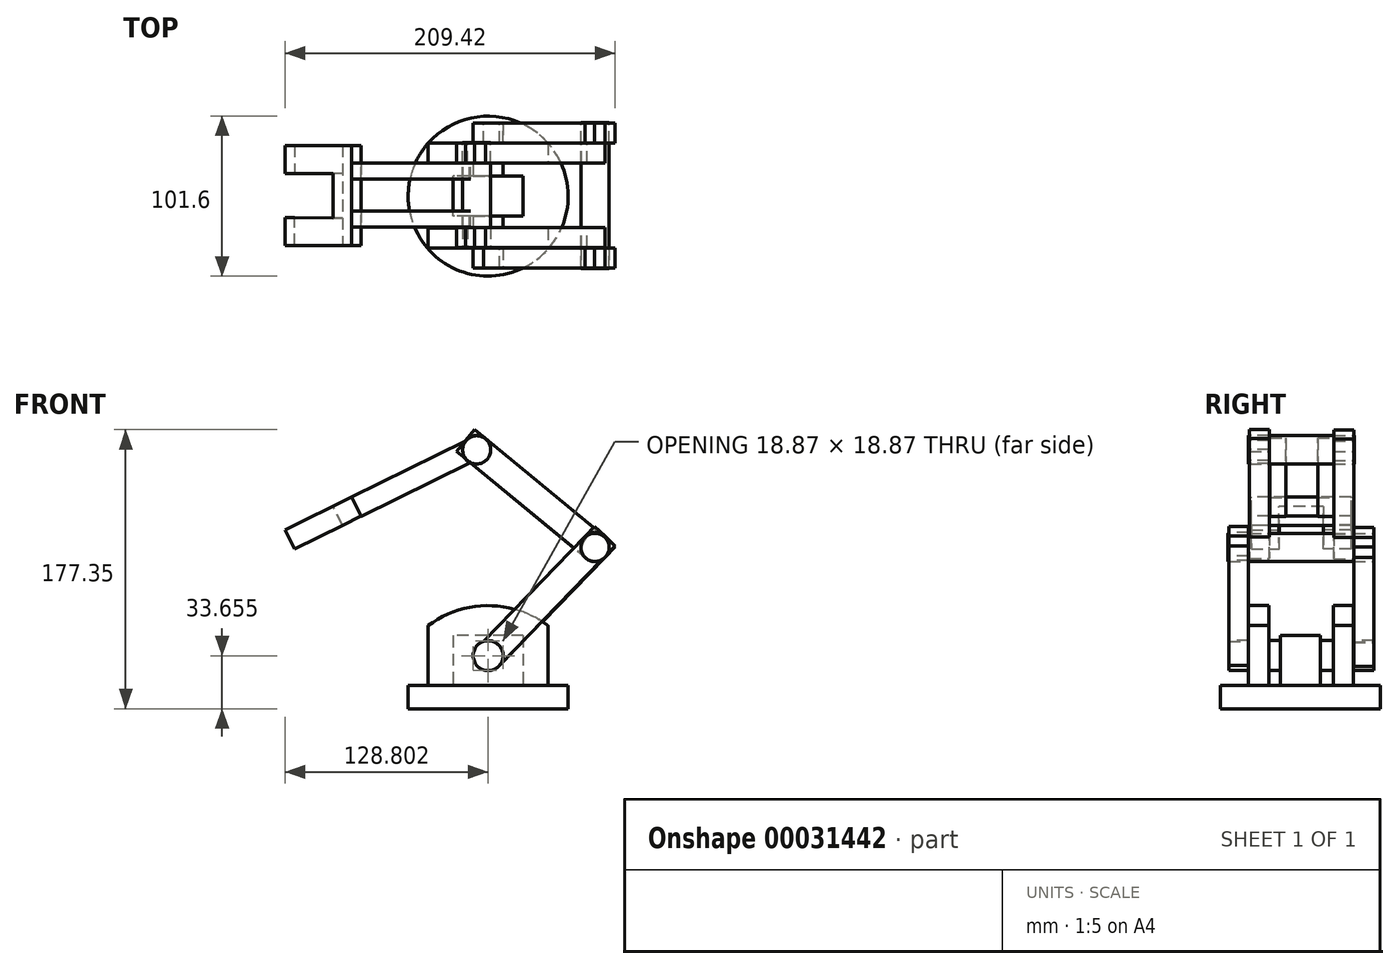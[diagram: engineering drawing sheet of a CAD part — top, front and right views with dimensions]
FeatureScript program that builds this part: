
annotation { "Feature Type Name" : "Feature", "Feature Type Description" : "" }
export const myFeature = defineFeature(function(context is Context, id is Id, definition is map)
    precondition{}
    {
        {
            var Q0;
            Q0=qCreatedBy(makeId("Top.planeOp"),FACE);
            var sketch = newSketch(context, id + "F0", { "sketchPlane" : qUnion([Q0])});
            skCircle(sketch, "E0", {"center": v(78.15, 35.6) * mm, "radius": 50.8 * mm});
            skSolve(sketch);
        }
        {
            var Q0;
            Q0 = qSketchRegion(id + "F0", true);
            extrude(context, id + "F1", {"entities" : qUnion([Q0]), "depth" : 14.7 * mm});
        }
        {
            var Q0;
            Q0=makeQuery(id+"F1.opExtrude","CAP_FACE",FACE,{"disambiguationData":[OSD([sQuery(id+"F0.wireOp",EDGE,"E0")])],"isStart":false});
            var sketch = newSketch(context, id + "F2", { "sketchPlane" : qUnion([Q0])});
            skLineSegment(sketch, "E1.bottom", {"start": v(40.05, 15.3) * mm, "end": v(116.25, 15.3) * mm});
            skLineSegment(sketch, "E1.top", {"start": v(40.05, 2.6) * mm, "end": v(116.25, 2.6) * mm});
            skLineSegment(sketch, "E1.left", {"start": v(40.05, 15.3) * mm, "end": v(40.05, 2.6) * mm});
            skLineSegment(sketch, "E1.right", {"start": v(116.25, 15.3) * mm, "end": v(116.25, 2.6) * mm});
            skLineSegment(sketch, "E2.bottom", {"start": v(40.05, 69.2) * mm, "end": v(116.25, 69.2) * mm});
            skLineSegment(sketch, "E2.top", {"start": v(40.05, 56.5) * mm, "end": v(116.25, 56.5) * mm});
            skLineSegment(sketch, "E2.left", {"start": v(40.05, 69.2) * mm, "end": v(40.05, 56.5) * mm});
            skLineSegment(sketch, "E2.right", {"start": v(116.25, 69.2) * mm, "end": v(116.25, 56.5) * mm});
            skSolve(sketch);
        }
        {
            var Q0;
            Q0 = qSketchRegion(id + "F2", true);
            extrude(context, id + "F3", {"entities" : qUnion([Q0]), "operationType" : NewBodyOperationType.ADD, "depth" : 38.1 * mm});
        }
        {
            var Q0;
            Q0=makeQuery(id+"F3.opExtrude","SWEPT_FACE",FACE,{"disambiguationData":[OSD([sQuery(id+"F2.wireOp",EDGE,"E1.top")])]});
            var sketch = newSketch(context, id + "F4", { "sketchPlane" : qUnion([Q0])});
            skArc(sketch, "E3", {"start": v(116.25, 52.8) * mm, "mid": v(78.15, 65.5) * mm, "end": v(40.05, 52.8) * mm});
            skSolve(sketch);
        }
        {
            var Q0;
            Q0 = qSketchRegion(id + "F4", true);
            var Q1;
            Q1=makeQuery(id+"F4.imprint","IMPRINT",FACE,{"disambiguationData":[TD([[makeQuery(id+"F4.imprint","IMPRINT",EDGE,{"derivedFrom":sQuery(id+"F4.wireOp",EDGE,"E3")}),1.0]])]});
            extrude(context, id + "F5", {"entities" : qUnion([Q0, Q1]), "operationType" : NewBodyOperationType.ADD, "oppositeDirection" : true, "depth" : 12.7 * mm});
        }
        {
            var Q0;
            Q0=makeQuery(id+"F3.opExtrude","SWEPT_FACE",FACE,{"disambiguationData":[OSD([sQuery(id+"F2.wireOp",EDGE,"E2.top")])]});
            var sketch = newSketch(context, id + "F6", { "sketchPlane" : qUnion([Q0])});
            skArc(sketch, "E4", {"start": v(116.25, 52.8) * mm, "mid": v(78.15, 65.5) * mm, "end": v(40.05, 52.8) * mm});
            skSolve(sketch);
        }
        {
            var Q0;
            Q0 = qSketchRegion(id + "F6", true);
            var Q1;
            Q1=makeQuery(id+"F6.imprint","IMPRINT",FACE,{"disambiguationData":[TD([[makeQuery(id+"F6.imprint","IMPRINT",EDGE,{"derivedFrom":sQuery(id+"F6.wireOp",EDGE,"E4")}),1.0]])]});
            extrude(context, id + "F7", {"entities" : qUnion([Q0, Q1]), "operationType" : NewBodyOperationType.ADD, "oppositeDirection" : true, "depth" : 12.7 * mm});
        }
        {
            var Q0;
            {var subQ0=sQuery(id+"F0.wireOp",EDGE,"E0");var subQ1=makeQuery(id+"F1.opExtrude","CAP_FACE",FACE,{"disambiguationData":[OSD([subQ0])],"isStart":false});Q0=makeQuery(id+"F3.boolean.opBoolean","SPLIT",FACE,{"disambiguationData":[TD([makeQuery(id+"F1.opExtrude","SWEPT_FACE",FACE,{"disambiguationData":[OSD([subQ0])]}),subQ1,makeQuery(id+"F3.opExtrude","SWEPT_FACE",FACE,{"disambiguationData":[OSD([sQuery(id+"F2.wireOp",EDGE,"E1.bottom")])]}),makeQuery(id+"F3.opExtrude","SWEPT_FACE",FACE,{"disambiguationData":[OSD([sQuery(id+"F2.wireOp",EDGE,"E1.top")])]}),makeQuery(id+"F3.opExtrude","SWEPT_FACE",FACE,{"disambiguationData":[OSD([sQuery(id+"F2.wireOp",EDGE,"E1.left")])]}),makeQuery(id+"F3.opExtrude","SWEPT_FACE",FACE,{"disambiguationData":[OSD([sQuery(id+"F2.wireOp",EDGE,"E1.right")])]}),makeQuery(id+"F3.opExtrude","SWEPT_FACE",FACE,{"disambiguationData":[OSD([sQuery(id+"F2.wireOp",EDGE,"E2.bottom")])]}),makeQuery(id+"F3.opExtrude","SWEPT_FACE",FACE,{"disambiguationData":[OSD([sQuery(id+"F2.wireOp",EDGE,"E2.top")])]}),makeQuery(id+"F3.opExtrude","SWEPT_FACE",FACE,{"disambiguationData":[OSD([sQuery(id+"F2.wireOp",EDGE,"E2.left")])]}),makeQuery(id+"F3.opExtrude","SWEPT_FACE",FACE,{"disambiguationData":[OSD([sQuery(id+"F2.wireOp",EDGE,"E2.right")])]})])],"derivedFrom":subQ1});}
            var sketch = newSketch(context, id + "F8", { "sketchPlane" : qUnion([Q0])});
            skPoint(sketch, "E5", {"position": v(78.15, 35.5) * mm});
            skLineSegment(sketch, "E6.rect.bottom", {"start": v(100.38, 22.8) * mm, "end": v(55.93, 22.8) * mm});
            skLineSegment(sketch, "E6.rect.top", {"start": v(100.38, 48.2) * mm, "end": v(55.93, 48.2) * mm});
            skLineSegment(sketch, "E6.rect.left", {"start": v(100.38, 22.8) * mm, "end": v(100.38, 48.2) * mm});
            skLineSegment(sketch, "E6.rect.right", {"start": v(55.93, 22.8) * mm, "end": v(55.93, 48.2) * mm});
            skSolve(sketch);
        }
        {
            var Q0;
            Q0 = qSketchRegion(id + "F8", true);
            extrude(context, id + "F9", {"entities" : qUnion([Q0]), "operationType" : NewBodyOperationType.ADD, "depth" : 31.75 * mm});
        }
        {
            var Q0;
            {var subQ0=sQuery(id+"F2.wireOp",EDGE,"E1.top");Q0=makeQuery(id+"F5.boolean.opBoolean","MERGE",FACE,{"derivedFrom":[makeQuery(id+"F3.opExtrude","SWEPT_FACE",FACE,{"disambiguationData":[OSD([subQ0])]}),makeQuery(id+"F5.opExtrude","CAP_FACE",FACE,{"disambiguationData":[OSD([subQ0,sQuery(id+"F4.wireOp",EDGE,"E3")])],"isStart":true})]});}
            var sketch = newSketch(context, id + "F10", { "sketchPlane" : qUnion([Q0])});
            skCircle(sketch, "E7", {"center": v(78.15, 33.75) * mm, "radius": 9.53 * mm});
            skSolve(sketch);
        }
        {
            var Q0;
            Q0 = qSketchRegion(id + "F10", true);
            extrude(context, id + "F11", {"entities" : qUnion([Q0]), "operationType" : NewBodyOperationType.REMOVE, "oppositeDirection" : true, "depth" : 68.25 * mm});
        }
        {
            var Q0;
            {var subQ0=sQuery(id+"F2.wireOp",EDGE,"E1.top");Q0=makeQuery(id+"F5.boolean.opBoolean","MERGE",FACE,{"derivedFrom":[makeQuery(id+"F3.opExtrude","SWEPT_FACE",FACE,{"disambiguationData":[OSD([subQ0])]}),makeQuery(id+"F5.opExtrude","CAP_FACE",FACE,{"disambiguationData":[OSD([subQ0,sQuery(id+"F4.wireOp",EDGE,"E3")])],"isStart":true})]});}
            var sketch = newSketch(context, id + "F12", { "sketchPlane" : qUnion([Q0])});
            skCircle(sketch, "E8", {"center": v(78.15, 33.75) * mm, "radius": 9.53 * mm});
            skSolve(sketch);
        }
        {
            var Q0;
            Q0 = qSketchRegion(id + "F12", true);
            extrude(context, id + "F13", {"entities" : qUnion([Q0]), "oppositeDirection" : true, "depth" : 66.7 * mm});
        }
        {
            var Q0;
            Q0=makeQuery(id+"F13.opExtrude","CAP_FACE",FACE,{"disambiguationData":[OSD([sQuery(id+"F12.wireOp",EDGE,"E8")])],"isStart":true});
            var sketch = newSketch(context, id + "F14", { "sketchPlane" : qUnion([Q0])});
            skCircle(sketch, "E9", {"center": v(78.15, 33.75) * mm, "radius": 9.53 * mm});
            skSolve(sketch);
        }
        {
            var Q0;
            Q0 = qSketchRegion(id + "F14", true);
            extrude(context, id + "F15", {"entities" : qUnion([Q0]), "operationType" : NewBodyOperationType.ADD, "depth" : 12.7 * mm});
        }
        {
            var Q0;
            Q0=makeQuery(id+"F13.opExtrude","CAP_FACE",FACE,{"disambiguationData":[OSD([sQuery(id+"F12.wireOp",EDGE,"E8")])],"isStart":false});
            var sketch = newSketch(context, id + "F16", { "sketchPlane" : qUnion([Q0])});
            skCircle(sketch, "E10", {"center": v(-78.15, 33.75) * mm, "radius": 9.53 * mm});
            skSolve(sketch);
        }
        {
            var Q0;
            Q0 = qSketchRegion(id + "F16", true);
            extrude(context, id + "F17", {"entities" : qUnion([Q0]), "operationType" : NewBodyOperationType.ADD, "depth" : 12.7 * mm});
        }
        {
            var Q0;
            {var subQ0=sQuery(id+"F2.wireOp",EDGE,"E1.top");Q0=makeQuery(id+"F5.boolean.opBoolean","MERGE",FACE,{"derivedFrom":[makeQuery(id+"F3.opExtrude","SWEPT_FACE",FACE,{"disambiguationData":[OSD([subQ0])]}),makeQuery(id+"F5.opExtrude","CAP_FACE",FACE,{"disambiguationData":[OSD([subQ0,sQuery(id+"F4.wireOp",EDGE,"E3")])],"isStart":true})]});}
            var sketch = newSketch(context, id + "F18", { "sketchPlane" : qUnion([Q0])});
            skLineSegment(sketch, "E11", {"start": v(75.19, 42.8) * mm, "end": v(145.78, 115.87) * mm});
            skLineSegment(sketch, "E12", {"start": v(145.78, 115.87) * mm, "end": v(158.68, 103.4) * mm});
            skLineSegment(sketch, "E13", {"start": v(158.68, 103.4) * mm, "end": v(84.64, 26.77) * mm});
            skSolve(sketch);
        }
        {
            var Q0;
            Q0 = qSketchRegion(id + "F18", true);
            var Q1;
            {var subQ5=sQuery(id+"F18.wireOp",EDGE,"E12");Q1=makeQuery(id+"F18.imprint","IMPRINT",FACE,{"disambiguationData":[TD([[makeQuery(id+"F18.imprint","IMPRINT",EDGE,{"derivedFrom":subQ5}),-1.0]])]});}
            var Q2;
            {var subQ0=makeQuery(id+"F11.boolean.opBoolean","COPY",EDGE,{"derivedFrom":makeQuery(id+"F11.opExtrude","CAP_EDGE",EDGE,{"disambiguationData":[OSD([sQuery(id+"F10.wireOp",EDGE,"E7")])],"isStart":true})});var subQ3=sQuery(id+"F18.wireOp",EDGE,"E11");var subQ4=makeQuery(id+"F18.imprint","INTERSECT",VERTEX,{"derivedFrom":[subQ0,subQ3]});Q2=makeQuery(id+"F18.imprint","IMPRINT",FACE,{"disambiguationData":[TD([[makeQuery(id+"F18.imprint","IMPRINT",EDGE,{"disambiguationData":[TD([[subQ4,-1.0]])],"derivedFrom":subQ3}),-1.0]])]});}
            extrude(context, id + "F19", {"entities" : qUnion([Q0, Q1, Q2]), "depth" : 12.7 * mm});
        }
        {
            var Q0;
            Q0=makeQuery(id+"F19.opExtrude","SWEPT_BODY",BODY,{"disambiguationData":[OSD([sQuery(id+"F10.wireOp",EDGE,"E7"),sQuery(id+"F18.wireOp",EDGE,"E11"),sQuery(id+"F18.wireOp",EDGE,"E12"),sQuery(id+"F18.wireOp",EDGE,"E13")])]});
            transform(context, id + "F20", {"entities" : qUnion([Q0]), "transformType" : TransformType.TRANSLATION_3D, "dx" : 0 * mm, "dy" : 79.44 * mm, "dz" : -0.68 * mm, "makeCopy" : true});
        }
        {
            var Q0;
            Q0=makeQuery(id+"F20.opPattern","COPY",FACE,{"derivedFrom":makeQuery(id+"F19.opExtrude","CAP_FACE",FACE,{"disambiguationData":[OSD([sQuery(id+"F10.wireOp",EDGE,"E7"),sQuery(id+"F18.wireOp",EDGE,"E11"),sQuery(id+"F18.wireOp",EDGE,"E12"),sQuery(id+"F18.wireOp",EDGE,"E13")])],"isStart":false}),"instanceName":"1"});
            var sketch = newSketch(context, id + "F21", { "sketchPlane" : qUnion([Q0])});
            skCircle(sketch, "E14", {"center": v(146, 102.51) * mm, "radius": 8.97 * mm});
            skSolve(sketch);
        }
        {
            var Q0;
            Q0 = qSketchRegion(id + "F21", true);
            extrude(context, id + "F22", {"entities" : qUnion([Q0]), "depth" : 79.74 * mm, "hasSecondDirection" : true, "secondDirectionOppositeDirection" : true, "secondDirectionDepth" : 12.92 * mm});
        }
        {
            var Q0;
            Q0=makeQuery(id+"F20.opPattern","COPY",FACE,{"derivedFrom":makeQuery(id+"F19.opExtrude","CAP_FACE",FACE,{"disambiguationData":[OSD([sQuery(id+"F10.wireOp",EDGE,"E7"),sQuery(id+"F18.wireOp",EDGE,"E11"),sQuery(id+"F18.wireOp",EDGE,"E12"),sQuery(id+"F18.wireOp",EDGE,"E13")])],"isStart":false}),"instanceName":"1"});
            var sketch = newSketch(context, id + "F23", { "sketchPlane" : qUnion([Q0])});
            skLineSegment(sketch, "E15", {"start": v(140.83, 95.15) * mm, "end": v(58.24, 163.3) * mm});
            skLineSegment(sketch, "E16", {"start": v(58.24, 163.3) * mm, "end": v(69.64, 177.1) * mm});
            skLineSegment(sketch, "E17", {"start": v(69.64, 177.1) * mm, "end": v(152.23, 108.96) * mm});
            skArc(sketch, "E18", {"start": v(152.23, 108.96) * mm, "mid": v(139.63, 107.75) * mm, "end": v(140.83, 95.15) * mm});
            skSolve(sketch);
        }
        {
            var Q0;
            Q0=makeQuery(id+"F23.imprint","IMPRINT",FACE,{"disambiguationData":[TD([[makeQuery(id+"F23.imprint","IMPRINT",EDGE,{"derivedFrom":sQuery(id+"F23.wireOp",EDGE,"2d7abb74-81f0-489b-a4b9-69b2d632399b")}),1.0]])]});
            var Q1;
            {var subQ5=sQuery(id+"F23.wireOp",EDGE,"E16");Q1=makeQuery(id+"F23.imprint","IMPRINT",FACE,{"disambiguationData":[TD([[makeQuery(id+"F23.imprint","IMPRINT",EDGE,{"derivedFrom":subQ5}),-1.0]])]});}
            var Q2;
            {var subQ5=sQuery(id+"F23.wireOp",EDGE,"E18");Q2=makeQuery(id+"F23.imprint","IMPRINT",FACE,{"disambiguationData":[TD([[makeQuery(id+"F23.imprint","IMPRINT",EDGE,{"derivedFrom":subQ5}),-1.0]])]});}
            extrude(context, id + "F24", {"entities" : qUnion([Q0, Q1, Q2]), "depth" : 12.7 * mm});
        }
        {
            var Q0;
            Q0=makeQuery(id+"F24.opExtrude","SWEPT_BODY",BODY,{"disambiguationData":[OSD([sQuery(id+"F23.wireOp",EDGE,"E15"),sQuery(id+"F23.wireOp",EDGE,"E16"),sQuery(id+"F23.wireOp",EDGE,"E17"),sQuery(id+"F23.wireOp",EDGE,"2d7abb74-81f0-489b-a4b9-69b2d632399b")])]});
            transform(context, id + "F25", {"entities" : qUnion([Q0]), "transformType" : TransformType.TRANSLATION_3D, "dx" : 0 * mm, "dy" : -53.6 * mm, "dz" : 0.24 * mm, "makeCopy" : true});
        }
        {
            var Q0;
            Q0=makeQuery(id+"F24.opExtrude","CAP_FACE",FACE,{"disambiguationData":[OSD([sQuery(id+"F23.wireOp",EDGE,"E15"),sQuery(id+"F23.wireOp",EDGE,"E16"),sQuery(id+"F23.wireOp",EDGE,"E17"),sQuery(id+"F23.wireOp",EDGE,"2d7abb74-81f0-489b-a4b9-69b2d632399b")])],"isStart":false});
            var sketch = newSketch(context, id + "F26", { "sketchPlane" : qUnion([Q0])});
            skCircle(sketch, "E19", {"center": v(70.84, 164.5) * mm, "radius": 8.95 * mm});
            skSolve(sketch);
        }
        {
            var Q0;
            Q0 = qSketchRegion(id + "F26", true);
            extrude(context, id + "F27", {"entities" : qUnion([Q0]), "depth" : 54.04 * mm, "hasSecondDirection" : true, "secondDirectionOppositeDirection" : true, "secondDirectionDepth" : 13.1 * mm});
        }
        {
            var Q0;
            Q0=makeQuery(id+"F24.opExtrude","CAP_FACE",FACE,{"disambiguationData":[OSD([sQuery(id+"F23.wireOp",EDGE,"E15"),sQuery(id+"F23.wireOp",EDGE,"E16"),sQuery(id+"F23.wireOp",EDGE,"E17"),sQuery(id+"F23.wireOp",EDGE,"2d7abb74-81f0-489b-a4b9-69b2d632399b")])],"isStart":false});
            var sketch = newSketch(context, id + "F28", { "sketchPlane" : qUnion([Q0])});
            skLineSegment(sketch, "E20", {"start": v(66.3, 156.25) * mm, "end": v(-2.6, 122.1) * mm});
            skLineSegment(sketch, "E21", {"start": v(-2.6, 122.1) * mm, "end": v(-8.65, 134.32) * mm});
            skLineSegment(sketch, "E22", {"start": v(-8.65, 134.32) * mm, "end": v(67.08, 171.86) * mm});
            skArc(sketch, "E23", {"start": v(67.08, 171.86) * mm, "mid": v(62.11, 164.28) * mm, "end": v(66.3, 156.25) * mm});
            skSolve(sketch);
        }
        {
            var Q0;
            Q0 = qSketchRegion(id + "F28", true);
            extrude(context, id + "F29", {"entities" : qUnion([Q0]), "depth" : 10.16 * mm});
        }
        {
            var Q0;
            Q0=makeQuery(id+"F29.opExtrude","SWEPT_BODY",BODY,{"disambiguationData":[OSD([sQuery(id+"F28.wireOp",EDGE,"E20"),sQuery(id+"F28.wireOp",EDGE,"E21"),sQuery(id+"F28.wireOp",EDGE,"E22"),sQuery(id+"F28.wireOp",EDGE,"31dbc0fa-8e11-4007-a332-41ba15a9be00")])]});
            transform(context, id + "F30", {"entities" : qUnion([Q0]), "transformType" : TransformType.TRANSLATION_3D, "dx" : 0 * mm, "dy" : -30.42 * mm, "dz" : 0 * mm, "makeCopy" : true});
        }
        {
            var Q0;
            Q0=makeQuery(id+"F29.opExtrude","SWEPT_FACE",FACE,{"disambiguationData":[OSD([sQuery(id+"F28.wireOp",EDGE,"E22")])]});
            var sketch = newSketch(context, id + "F31", { "sketchPlane" : qUnion([Q0])});
            skLineSegment(sketch, "E24.bottom", {"start": v(38.9, 67.77) * mm, "end": v(52.1, 67.77) * mm});
            skLineSegment(sketch, "E24.top", {"start": v(38.9, 4.27) * mm, "end": v(52.1, 4.27) * mm});
            skLineSegment(sketch, "E24.left", {"start": v(38.9, 67.77) * mm, "end": v(38.9, 4.27) * mm});
            skLineSegment(sketch, "E24.right", {"start": v(52.1, 67.77) * mm, "end": v(52.1, 4.27) * mm});
            skSolve(sketch);
        }
        {
            var Q0;
            Q0 = qSketchRegion(id + "F31", true);
            extrude(context, id + "F32", {"entities" : qUnion([Q0]), "oppositeDirection" : true, "depth" : 13.44 * mm});
        }
        {
            var Q0;
            Q0=makeQuery(id+"F32.opExtrude","CAP_FACE",FACE,{"disambiguationData":[OSD([sQuery(id+"F31.wireOp",EDGE,"E24.bottom"),sQuery(id+"F31.wireOp",EDGE,"E24.top"),sQuery(id+"F31.wireOp",EDGE,"E24.left"),sQuery(id+"F31.wireOp",EDGE,"E24.right")])],"isStart":true});
            var sketch = newSketch(context, id + "F33", { "sketchPlane" : qUnion([Q0])});
            skLineSegment(sketch, "E25", {"start": v(55.73, 21.63) * mm, "end": v(55.73, 4.27) * mm});
            skLineSegment(sketch, "E26", {"start": v(55.73, 4.27) * mm, "end": v(4.93, 4.27) * mm});
            skLineSegment(sketch, "E27", {"start": v(4.93, 4.27) * mm, "end": v(4.93, 22.05) * mm});
            skLineSegment(sketch, "E28", {"start": v(4.93, 22.05) * mm, "end": v(55.73, 21.63) * mm});
            skSolve(sketch);
        }
        {
            var Q0;
            {var subQ5=sQuery(id+"F33.wireOp",EDGE,"E27");Q0=makeQuery(id+"F33.imprint","IMPRINT",FACE,{"disambiguationData":[TD([[makeQuery(id+"F33.imprint","IMPRINT",EDGE,{"derivedFrom":subQ5}),-1.0]])]});}
            extrude(context, id + "F34", {"entities" : qUnion([Q0]), "operationType" : NewBodyOperationType.ADD, "oppositeDirection" : true, "depth" : 13.42 * mm});
        }
        {
            var Q0;
            {var subQ0=sQuery(id+"F31.wireOp",EDGE,"E24.left");Q0=makeQuery(id+"F34.boolean.opBoolean","MERGE",FACE,{"derivedFrom":[makeQuery(id+"F32.opExtrude","CAP_FACE",FACE,{"disambiguationData":[OSD([sQuery(id+"F31.wireOp",EDGE,"E24.bottom"),sQuery(id+"F31.wireOp",EDGE,"E24.top"),subQ0,sQuery(id+"F31.wireOp",EDGE,"E24.right")])],"isStart":true}),makeQuery(id+"F34.opExtrude","CAP_FACE",FACE,{"disambiguationData":[OSD([subQ0,sQuery(id+"F33.wireOp",EDGE,"E26"),sQuery(id+"F33.wireOp",EDGE,"E27"),sQuery(id+"F33.wireOp",EDGE,"E28")])],"isStart":true})]});}
            var sketch = newSketch(context, id + "F35", { "sketchPlane" : qUnion([Q0])});
            skLineSegment(sketch, "E29.bottom", {"start": v(55.77, 67.77) * mm, "end": v(4.97, 67.77) * mm});
            skLineSegment(sketch, "E29.top", {"start": v(55.77, 50) * mm, "end": v(4.97, 50) * mm});
            skLineSegment(sketch, "E29.left", {"start": v(55.77, 67.77) * mm, "end": v(55.77, 50) * mm});
            skLineSegment(sketch, "E29.right", {"start": v(4.97, 67.77) * mm, "end": v(4.97, 50) * mm});
            skSolve(sketch);
        }
        {
            var Q0;
            {var subQ5=sQuery(id+"F35.wireOp",EDGE,"E29.right");Q0=makeQuery(id+"F35.imprint","IMPRINT",FACE,{"disambiguationData":[TD([[makeQuery(id+"F35.imprint","IMPRINT",EDGE,{"derivedFrom":subQ5}),1.0]])]});}
            extrude(context, id + "F36", {"entities" : qUnion([Q0]), "operationType" : NewBodyOperationType.ADD, "oppositeDirection" : true, "depth" : 13.32 * mm});
        }
        {
            var Q0;
            Q0=makeQuery(id+"F19.opExtrude","CAP_FACE",FACE,{"disambiguationData":[OSD([sQuery(id+"F10.wireOp",EDGE,"E7"),sQuery(id+"F18.wireOp",EDGE,"E11"),sQuery(id+"F18.wireOp",EDGE,"E12"),sQuery(id+"F18.wireOp",EDGE,"E13")])],"isStart":false});
            var sketch = newSketch(context, id + "F37", { "sketchPlane" : qUnion([Q0])});
            skCircle(sketch, "E30", {"center": v(146, 103.19) * mm, "radius": 8.97 * mm});
            skSolve(sketch);
        }
        {
            var Q0;
            Q0 = qSketchRegion(id + "F37", true);
            extrude(context, id + "F38", {"entities" : qUnion([Q0]), "operationType" : NewBodyOperationType.REMOVE, "oppositeDirection" : true, "depth" : 12.7 * mm});
        }
        {
            var Q0;
            Q0=makeQuery(id+"F20.opPattern","COPY",FACE,{"derivedFrom":makeQuery(id+"F19.opExtrude","CAP_FACE",FACE,{"disambiguationData":[OSD([sQuery(id+"F10.wireOp",EDGE,"E7"),sQuery(id+"F18.wireOp",EDGE,"E11"),sQuery(id+"F18.wireOp",EDGE,"E12"),sQuery(id+"F18.wireOp",EDGE,"E13")])],"isStart":true}),"instanceName":"1"});
            var sketch = newSketch(context, id + "F39", { "sketchPlane" : qUnion([Q0])});
            skCircle(sketch, "E31", {"center": v(-146, 102.51) * mm, "radius": 8.97 * mm});
            skSolve(sketch);
        }
        {
            var Q0;
            Q0 = qSketchRegion(id + "F39", true);
            extrude(context, id + "F40", {"entities" : qUnion([Q0]), "operationType" : NewBodyOperationType.REMOVE, "oppositeDirection" : true, "depth" : 12.7 * mm});
        }
        {
            var Q0;
            Q0=makeQuery(id+"F25.opPattern","COPY",FACE,{"derivedFrom":makeQuery(id+"F24.opExtrude","CAP_FACE",FACE,{"disambiguationData":[OSD([sQuery(id+"F23.wireOp",EDGE,"E15"),sQuery(id+"F23.wireOp",EDGE,"E16"),sQuery(id+"F23.wireOp",EDGE,"E17"),sQuery(id+"F23.wireOp",EDGE,"2d7abb74-81f0-489b-a4b9-69b2d632399b")])],"isStart":false}),"instanceName":"1"});
            var sketch = newSketch(context, id + "F41", { "sketchPlane" : qUnion([Q0])});
            skCircle(sketch, "E32", {"center": v(70.84, 164.74) * mm, "radius": 8.95 * mm});
            skSolve(sketch);
        }
        {
            var Q0;
            Q0 = qSketchRegion(id + "F41", true);
            extrude(context, id + "F42", {"entities" : qUnion([Q0]), "operationType" : NewBodyOperationType.REMOVE, "oppositeDirection" : true, "depth" : 12.7 * mm});
        }
        {
            var Q0;
            Q0=makeQuery(id+"F24.opExtrude","CAP_FACE",FACE,{"disambiguationData":[OSD([sQuery(id+"F23.wireOp",EDGE,"E15"),sQuery(id+"F23.wireOp",EDGE,"E16"),sQuery(id+"F23.wireOp",EDGE,"E17"),sQuery(id+"F23.wireOp",EDGE,"2d7abb74-81f0-489b-a4b9-69b2d632399b")])],"isStart":true});
            var sketch = newSketch(context, id + "F43", { "sketchPlane" : qUnion([Q0])});
            skCircle(sketch, "E33", {"center": v(-70.84, 164.5) * mm, "radius": 8.95 * mm});
            skSolve(sketch);
        }
        {
            var Q0;
            Q0 = qSketchRegion(id + "F43", true);
            extrude(context, id + "F44", {"entities" : qUnion([Q0]), "operationType" : NewBodyOperationType.REMOVE, "oppositeDirection" : true, "depth" : 12.7 * mm});
        }
    });
